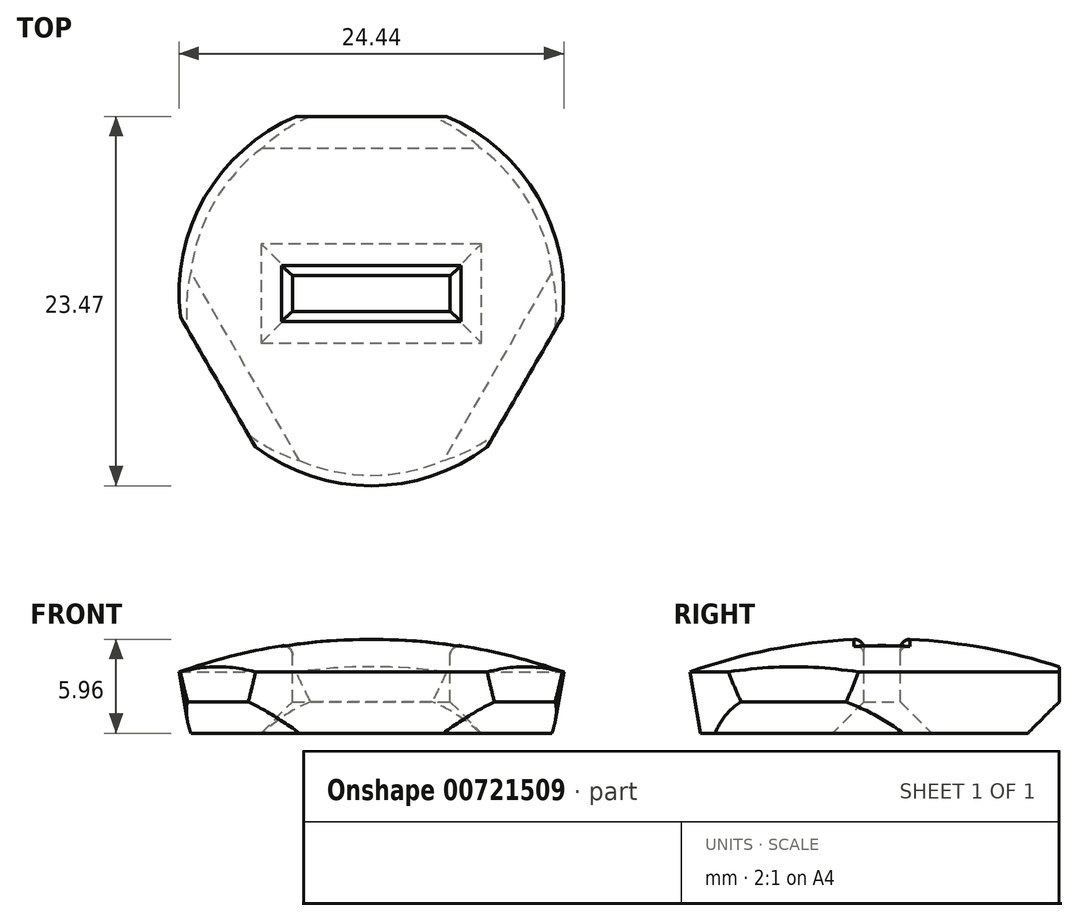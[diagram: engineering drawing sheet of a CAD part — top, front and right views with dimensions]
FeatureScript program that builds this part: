
annotation { "Feature Type Name" : "Feature", "Feature Type Description" : "" }
export const myFeature = defineFeature(function(context is Context, id is Id, definition is map)
    precondition{}
    {
        {
            var Q0;
            Q0=qCreatedBy(makeId("Front.planeOp"),FACE);
            var sketch = newSketch(context, id + "F0", { "sketchPlane" : qUnion([Q0])});
            skLineSegment(sketch, "E0", {"start": v(0, 0) * mm, "end": v(20, 0) * mm});
            skArc(sketch, "E1", {"start": v(20, 0) * mm, "mid": v(10.44, 4.47) * mm, "end": v(0, 6) * mm});
            skLineSegment(sketch, "E2", {"start": v(0, 6) * mm, "end": v(0, 0) * mm});
            skSolve(sketch);
        }
        {
            var Q0;
            Q0=makeQuery(id+"F0.imprint","IMPRINT",FACE,{"disambiguationData":[TD([[makeQuery(id+"F0.imprint","IMPRINT",EDGE,{"derivedFrom":sQuery(id+"F0.wireOp",EDGE,"E0")}),1.0]])]});
            var Q1;
            Q1=sQuery(id+"F0.wireOp",EDGE,"E2");
            revolve(context, id + "F1", {"surfaceOperationType" : NewSurfaceOperationType.NEW, "entities" : qUnion([Q0]), "axis" : qUnion([Q1]), "revolveType" : RevolveType.FULL});
        }
        {
            var Q0;
            Q0=qCreatedBy(makeId("Top.planeOp"),FACE);
            cPlane(context, id + "F2", {"entities" : qUnion([Q0]), "cplaneType" : CPlaneType.OFFSET, "offset" : 9.39 * mm, "width" : 150 * mm, "height" : 150 * mm});
        }
        {
            var Q0;
            Q0=qCreatedBy(id+"F2.planeOp",FACE);
            var sketch = newSketch(context, id + "F3", { "sketchPlane" : qUnion([Q0])});
            skLineSegment(sketch, "E3.bottom", {"start": v(-5, 1.15) * mm, "end": v(5, 1.15) * mm});
            skLineSegment(sketch, "E3.top", {"start": v(-5, -1.15) * mm, "end": v(5, -1.15) * mm});
            skLineSegment(sketch, "E3.left", {"start": v(-5, 1.15) * mm, "end": v(-5, -1.15) * mm});
            skLineSegment(sketch, "E3.right", {"start": v(5, 1.15) * mm, "end": v(5, -1.15) * mm});
            skPoint(sketch, "E3.middle", {"position": v(0, 0) * mm});
            skSolve(sketch);
        }
        {
            var Q0;
            Q0=makeQuery(id+"F3.imprint","IMPRINT",FACE,{"disambiguationData":[TD([[makeQuery(id+"F3.imprint","IMPRINT",EDGE,{"derivedFrom":sQuery(id+"F3.wireOp",EDGE,"E3.bottom")}),-1.0]])]});
            extrude(context, id + "F4", {"entities" : qUnion([Q0]), "operationType" : NewBodyOperationType.REMOVE, "oppositeDirection" : true, "depth" : 25 * mm, "offsetDistance" : 25 * mm});
        }
        {
            var Q0;
            Q0=makeQuery(id+"F1.opRevolve","SWEPT_FACE",FACE,{"disambiguationData":[OSD([sQuery(id+"F0.wireOp",EDGE,"E0")])]});
            var sketch = newSketch(context, id + "F5", { "sketchPlane" : qUnion([Q0])});
            skCircle(sketch, "E4.cCircle", {"center": v(0, 0) * mm, "radius": 22.5 * mm, "construction": true});
            skPoint(sketch, "E4.cCircle.perimeterSnap0", {"position": v(0, 1.15) * mm});
            skLineSegment(sketch, "E4.0", {"start": v(0, 22.5) * mm, "end": v(19.49, -11.25) * mm});
            skPoint(sketch, "E4.0.startSnap0", {"position": v(0, 1.15) * mm});
            skLineSegment(sketch, "E4.1", {"start": v(19.49, -11.25) * mm, "end": v(-19.49, -11.25) * mm});
            skLineSegment(sketch, "E4.2", {"start": v(-19.49, -11.25) * mm, "end": v(0, 22.5) * mm});
            skSolve(sketch);
        }
        {
            var Q0;
            {var subQ1=sQuery(id+"F0.wireOp",EDGE,"E0");var subQ2=makeQuery(id+"F1.opRevolve","SWEPT_FACE",FACE,{"disambiguationData":[OSD([subQ1])]});var subQ8=subQ2;Q0=makeQuery(id+"F5.imprint","IMPRINT",FACE,{"disambiguationData":[TD([[makeQuery(id+"F5.imprint","IMPRINT",EDGE,{"derivedFrom":makeQuery(id+"F4.boolean.opBoolean","INTERSECT",EDGE,{"derivedFrom":[subQ8,makeQuery(id+"F4.opExtrude","SWEPT_FACE",FACE,{"disambiguationData":[OSD([sQuery(id+"F3.wireOp",EDGE,"E3.bottom")])]})]})}),-1.0]])]});}
            extrude(context, id + "F6", {"entities" : qUnion([Q0]), "operationType" : NewBodyOperationType.INTERSECT, "oppositeDirection" : true, "depth" : 25 * mm, "offsetDistance" : 25 * mm});
        }
        {
            var Q0;
            Q0=makeQuery(id+"F1.opRevolve","SWEPT_FACE",FACE,{"disambiguationData":[OSD([sQuery(id+"F0.wireOp",EDGE,"E0")])]});
            chamfer(context, id + "F7", {"entities" : qUnion([Q0]), "width" : 2 * mm, "tangentPropagation" : true});
        }
        {
            var Q0;
            Q0=makeQuery(id+"F4.boolean.opBoolean","INTERSECT",EDGE,{"derivedFrom":[makeQuery(id+"F1.opRevolve","SWEPT_FACE",FACE,{"disambiguationData":[OSD([sQuery(id+"F0.wireOp",EDGE,"E1")])]}),makeQuery(id+"F4.opExtrude","SWEPT_FACE",FACE,{"disambiguationData":[OSD([sQuery(id+"F3.wireOp",EDGE,"E3.bottom")])]})]});
            var Q1;
            Q1=makeQuery(id+"F4.boolean.opBoolean","INTERSECT",EDGE,{"derivedFrom":[makeQuery(id+"F1.opRevolve","SWEPT_FACE",FACE,{"disambiguationData":[OSD([sQuery(id+"F0.wireOp",EDGE,"E1")])]}),makeQuery(id+"F4.opExtrude","SWEPT_FACE",FACE,{"disambiguationData":[OSD([sQuery(id+"F3.wireOp",EDGE,"E3.top")])]})]});
            var Q2;
            Q2=makeQuery(id+"F4.boolean.opBoolean","INTERSECT",EDGE,{"derivedFrom":[makeQuery(id+"F1.opRevolve","SWEPT_FACE",FACE,{"disambiguationData":[OSD([sQuery(id+"F0.wireOp",EDGE,"E1")])]}),makeQuery(id+"F4.opExtrude","SWEPT_FACE",FACE,{"disambiguationData":[OSD([sQuery(id+"F3.wireOp",EDGE,"E3.right")])]})]});
            var Q3;
            Q3=makeQuery(id+"F4.boolean.opBoolean","INTERSECT",EDGE,{"derivedFrom":[makeQuery(id+"F1.opRevolve","SWEPT_FACE",FACE,{"disambiguationData":[OSD([sQuery(id+"F0.wireOp",EDGE,"E1")])]}),makeQuery(id+"F4.opExtrude","SWEPT_FACE",FACE,{"disambiguationData":[OSD([sQuery(id+"F3.wireOp",EDGE,"E3.left")])]})]});
            fillet(context, id + "F8", {"entities" : qUnion([Q0, Q1, Q2, Q3]), "tangentPropagation" : true, "radius" : 0.6 * mm, "defaultsChanged" : true, "vertexSettings" : [], "allowEdgeOverflow" : false});
        }
    });
